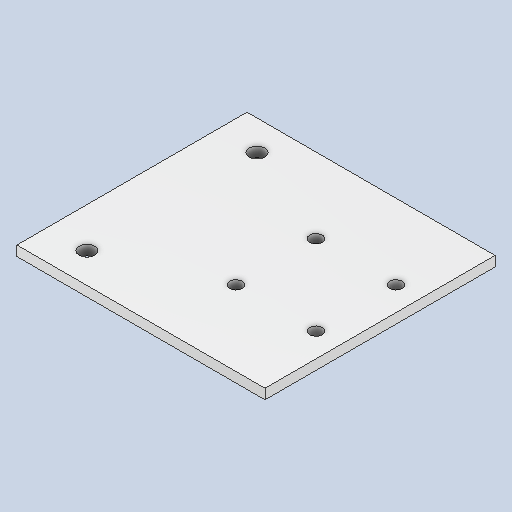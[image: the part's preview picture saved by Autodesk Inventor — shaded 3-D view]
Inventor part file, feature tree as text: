
AUTODESK INVENTOR PART (.ipt)
format: ipt  version: 2023 (Build 270158000, 158)  size: 108,032 bytes
history: native  units: in
note: dims shown in document units (in); Inventor stores cm internally (conversion verified against a paired STEP export)
features: other x3, sketch x2
ambient origin geometry x8: Origin, YZ Plane, XZ Plane, XY Plane, X Axis, Y Axis, Z Axis, Center Point
bodies: Solid1 (feature_tree)
feature tree (5):
  other  "MotorMount.ipt"
  other  "Solid1::MotorMount.ipt"
  other  "TaggingFeature1"
  sketch  "Sketch1"  dims[d0=0.3937in]
  sketch  "Sketch2"
